# Revit family: FantiniCosmi_BIM_AP20050
name_source: partatom
category: Generic Models
units: mm (PartAtom-declared; Revit-internal decimal feet)

## family parameters
Always vertical = Yes
Can host rebar = No
Cut with Voids When Loaded = No
Part Type = Normal
Room Calculation Point = No
Round Connector Dimension = Use Diameter
Shared = No
Work Plane-Based = No

## types (1)
- Standard
    Average Sound Pressure (Lp) 1Mt = 42.1 dB(A)
    Average Sound Pressure (Lp) 3Mt = 34.7 dB(A)
    Default Elevation = 0 mm  [stored 0 ft]
    Description = HRP DOMO 10 Z
    Fan Number = 2
    Filteration Class = ePM1  80%
    Heat Recovery Efficiency = 85.2 %
    Max Flow = 140 mc/h
    Part Number = AP20050
    Pressure = 100 Pa
    Sound Power (Lw) from body = 49 dB(A)
    Sound Power (Lw) from channels = 54 dB(A)
    Weight = 32 Kg

note: [stored X ft] marks values corroborated as IEEE doubles in the binary element streams (Revit-internal decimal feet)

## geometry (parser evidence)
native form markers: Sweep x3
no freeform markers — native parametric forms only
